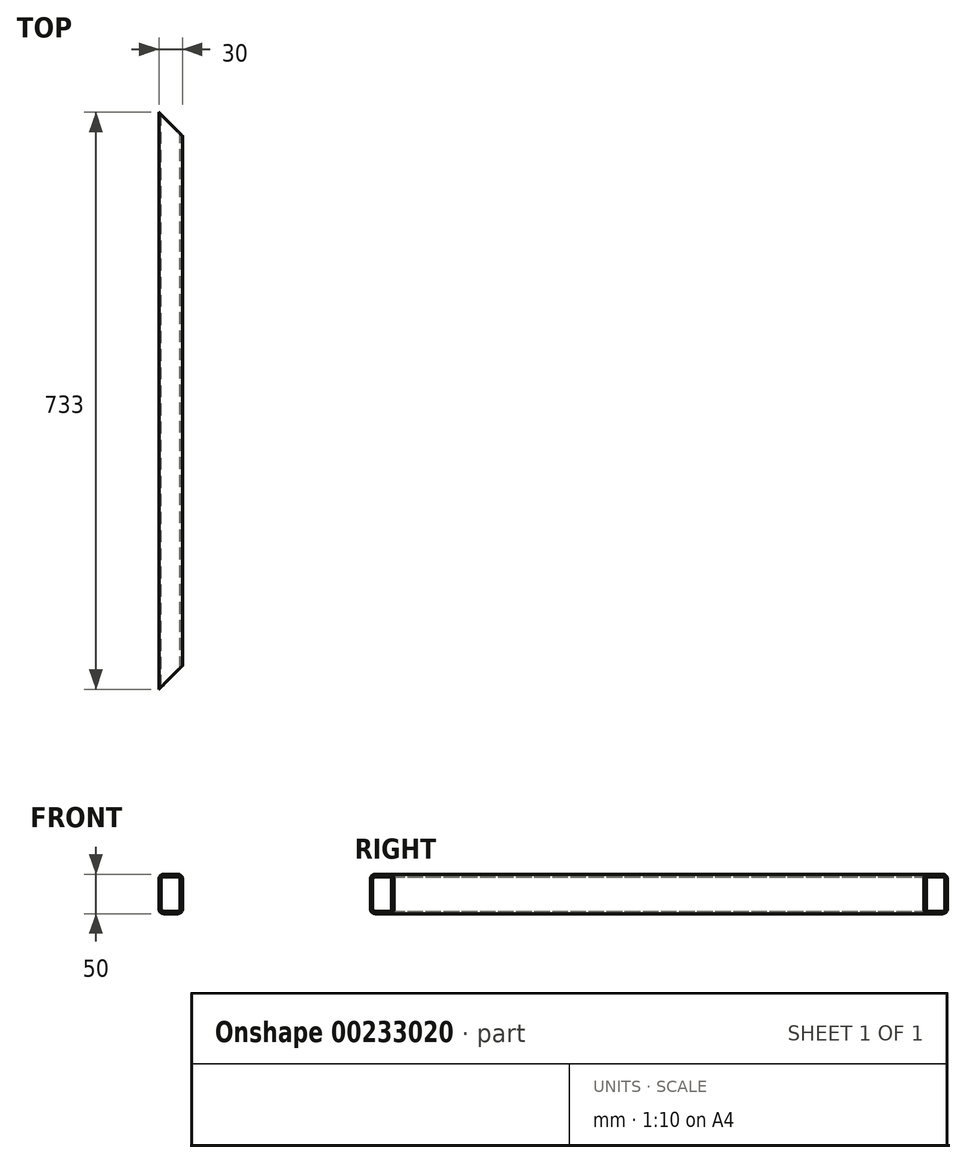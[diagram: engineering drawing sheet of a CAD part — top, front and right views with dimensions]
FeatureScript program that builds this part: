
annotation { "Feature Type Name" : "Feature", "Feature Type Description" : "" }
export const myFeature = defineFeature(function(context is Context, id is Id, definition is map)
    precondition{}
    {
        {
            var Q0;
            Q0=qCreatedBy(makeId("Front.planeOp"),FACE);
            var sketch = newSketch(context, id + "F0", { "sketchPlane" : qUnion([Q0])});
            skLineSegment(sketch, "E0.bottom", {"start": v(9, 25) * mm, "end": v(-9, 25) * mm});
            skLineSegment(sketch, "E0.top", {"start": v(9, -25) * mm, "end": v(-9, -25) * mm});
            skLineSegment(sketch, "E0.left", {"start": v(15, 19) * mm, "end": v(15, -19) * mm});
            skLineSegment(sketch, "E0.right", {"start": v(-15, 19) * mm, "end": v(-15, -19) * mm});
            skPoint(sketch, "E0.middle", {"position": v(0, 0) * mm});
            skPoint(sketch, "E1.visualSharp", {"position": v(-15, 25) * mm});
            skArc(sketch, "E1.filletArc", {"start": v(-9, 25) * mm, "mid": v(-13.24, 23.24) * mm, "end": v(-15, 19) * mm});
            skPoint(sketch, "E2.visualSharp", {"position": v(-15, -25) * mm});
            skArc(sketch, "E2.filletArc", {"start": v(-15, -19) * mm, "mid": v(-13.24, -23.24) * mm, "end": v(-9, -25) * mm});
            skPoint(sketch, "E3.visualSharp", {"position": v(15, -25) * mm});
            skArc(sketch, "E3.filletArc", {"start": v(9, -25) * mm, "mid": v(13.24, -23.24) * mm, "end": v(15, -19) * mm});
            skPoint(sketch, "E4.visualSharp", {"position": v(15, 25) * mm});
            skArc(sketch, "E4.filletArc", {"start": v(15, 19) * mm, "mid": v(13.24, 23.24) * mm, "end": v(9, 25) * mm});
            skLineSegment(sketch, "E5.0", {"start": v(9, 22) * mm, "end": v(-9, 22) * mm});
            skArc(sketch, "E5.1", {"start": v(12, 19) * mm, "mid": v(11.12, 21.12) * mm, "end": v(9, 22) * mm});
            skArc(sketch, "E5.2", {"start": v(-9, 22) * mm, "mid": v(-11.12, 21.12) * mm, "end": v(-12, 19) * mm});
            skLineSegment(sketch, "E5.3", {"start": v(12, 19) * mm, "end": v(12, -19) * mm});
            skLineSegment(sketch, "E5.4", {"start": v(-12, 19) * mm, "end": v(-12, -19) * mm});
            skArc(sketch, "E5.5", {"start": v(-12, -19) * mm, "mid": v(-11.12, -21.12) * mm, "end": v(-9, -22) * mm});
            skLineSegment(sketch, "E5.6", {"start": v(9, -22) * mm, "end": v(-9, -22) * mm});
            skArc(sketch, "E5.7", {"start": v(9, -22) * mm, "mid": v(11.12, -21.12) * mm, "end": v(12, -19) * mm});
            skSolve(sketch);
        }
        {
            var Q0;
            Q0=makeQuery(id+"F0.imprint","IMPRINT",FACE,{"disambiguationData":[TD([[makeQuery(id+"F0.imprint","IMPRINT",EDGE,{"derivedFrom":sQuery(id+"F0.wireOp",EDGE,"E0.bottom")}),1.0]])]});
            extrude(context, id + "F1", {"entities" : qUnion([Q0]), "endBound" : BoundingType.SYMMETRIC, "depth" : 733 * mm});
        }
        {
            var Q0;
            Q0=makeQuery(id+"F1.opExtrude","SWEPT_FACE",FACE,{"disambiguationData":[OSD([sQuery(id+"F0.wireOp",EDGE,"E0.bottom")])]});
            var sketch = newSketch(context, id + "F2", { "sketchPlane" : qUnion([Q0])});
            skLineSegment(sketch, "E6.left", {"start": v(15, 336.5) * mm, "end": v(15, 366.5) * mm});
            skPoint(sketch, "E6.middle", {"position": v(0, 366.5) * mm});
            skLineSegment(sketch, "E7", {"start": v(15, 336.5) * mm, "end": v(-15, 366.5) * mm});
            skLineSegment(sketch, "E8", {"start": v(-15, 366.5) * mm, "end": v(15, 366.5) * mm});
            skPoint(sketch, "E8.endSnap0", {"position": v(15, 366.5) * mm});
            skPoint(sketch, "E9.orphan", {"position": v(17.67, 366.5) * mm});
            skPoint(sketch, "E6.top.end.orphan", {"position": v(-15, 396.5) * mm});
            skPoint(sketch, "E6.top.start.orphan", {"position": v(15, 396.5) * mm});
            skPoint(sketch, "E6.right.start.orphan", {"position": v(-15, 336.5) * mm});
            skLineSegment(sketch, "E10.MirrorCS", {"start": v(-15, -366.5) * mm, "end": v(15, -366.5) * mm});
            skPoint(sketch, "E11.MirrorP", {"position": v(17.67, -366.5) * mm});
            skPoint(sketch, "E12.MirrorP", {"position": v(-15, -336.5) * mm});
            skLineSegment(sketch, "E13.MirrorCS", {"start": v(15, -336.5) * mm, "end": v(15, -366.5) * mm});
            skLineSegment(sketch, "E14.MirrorCS", {"start": v(15, -336.5) * mm, "end": v(-15, -366.5) * mm});
            skPoint(sketch, "E15.MirrorP", {"position": v(15, -366.5) * mm});
            skPoint(sketch, "E16.MirrorP", {"position": v(0, -366.5) * mm});
            skSolve(sketch);
        }
        {
            var Q0;
            {var subQ0=sQuery(id+"F2.wireOp",EDGE,"E10.MirrorCS");var subQ1=makeQuery(id+"F1.opExtrude","SWEPT_EDGE",EDGE,{"disambiguationData":[OSD([sQuery(id+"F0.wireOp",EDGE,"E0.bottom"),sQuery(id+"F0.wireOp",EDGE,"E1.filletArc")])]});var subQ2=makeQuery(id+"F2.imprint","INTERSECT",VERTEX,{"derivedFrom":[subQ1,subQ0]});var subQ3=sQuery(id+"F2.wireOp",EDGE,"E14.MirrorCS");var subQ4=makeQuery(id+"F2.imprint","INTERSECT",VERTEX,{"derivedFrom":[subQ0,subQ3]});Q0=makeQuery(id+"F2.imprint","IMPRINT",FACE,{"disambiguationData":[TD([[makeQuery(id+"F2.imprint","IMPRINT",EDGE,{"disambiguationData":[TD([[subQ2,1.0],[subQ4,-1.0]])],"derivedFrom":subQ0}),1.0]])]});}
            var Q1;
            {var subQ0=sQuery(id+"F2.wireOp",EDGE,"E10.MirrorCS");var subQ1=sQuery(id+"F0.wireOp",EDGE,"E0.bottom");var subQ2=makeQuery(id+"F1.opExtrude","SWEPT_EDGE",EDGE,{"disambiguationData":[OSD([subQ1,sQuery(id+"F0.wireOp",EDGE,"E4.filletArc")])]});var subQ3=makeQuery(id+"F2.imprint","INTERSECT",VERTEX,{"derivedFrom":[subQ2,subQ0]});var subQ4=makeQuery(id+"F1.opExtrude","SWEPT_EDGE",EDGE,{"disambiguationData":[OSD([subQ1,sQuery(id+"F0.wireOp",EDGE,"E1.filletArc")])]});var subQ5=makeQuery(id+"F2.imprint","INTERSECT",VERTEX,{"derivedFrom":[subQ4,subQ0]});Q1=makeQuery(id+"F2.imprint","IMPRINT",FACE,{"disambiguationData":[TD([[makeQuery(id+"F2.imprint","IMPRINT",EDGE,{"disambiguationData":[TD([[subQ3,-1.0],[subQ5,1.0]])],"derivedFrom":subQ0}),-1.0]])]});}
            var Q2;
            {var subQ3=sQuery(id+"F2.wireOp",EDGE,"E13.MirrorCS");Q2=makeQuery(id+"F2.imprint","IMPRINT",FACE,{"disambiguationData":[TD([[makeQuery(id+"F2.imprint","IMPRINT",EDGE,{"derivedFrom":subQ3}),-1.0]])]});}
            var Q3;
            {var subQ0=sQuery(id+"F2.wireOp",EDGE,"E8");var subQ1=sQuery(id+"F2.wireOp",EDGE,"E7");var subQ2=makeQuery(id+"F2.imprint","INTERSECT",VERTEX,{"derivedFrom":[subQ1,subQ0]});Q3=makeQuery(id+"F2.imprint","IMPRINT",FACE,{"disambiguationData":[TD([[makeQuery(id+"F2.imprint","IMPRINT",EDGE,{"disambiguationData":[TD([[subQ2,1.0]])],"derivedFrom":subQ1}),-1.0]])]});}
            var Q4;
            {var subQ0=sQuery(id+"F2.wireOp",EDGE,"E7");var subQ1=sQuery(id+"F0.wireOp",EDGE,"E0.bottom");var subQ2=makeQuery(id+"F1.opExtrude","SWEPT_EDGE",EDGE,{"disambiguationData":[OSD([subQ1,sQuery(id+"F0.wireOp",EDGE,"E4.filletArc")])]});var subQ3=makeQuery(id+"F2.imprint","INTERSECT",VERTEX,{"derivedFrom":[subQ2,subQ0]});Q4=makeQuery(id+"F2.imprint","IMPRINT",FACE,{"disambiguationData":[TD([[makeQuery(id+"F2.imprint","IMPRINT",EDGE,{"disambiguationData":[TD([[subQ3,-1.0]])],"derivedFrom":subQ0}),-1.0]])]});}
            var Q5;
            {var subQ0=sQuery(id+"F2.wireOp",EDGE,"E6.left");Q5=makeQuery(id+"F2.imprint","IMPRINT",FACE,{"disambiguationData":[TD([[makeQuery(id+"F2.imprint","IMPRINT",EDGE,{"derivedFrom":subQ0}),1.0]])]});}
            var Q6;
            Q6=makeQuery(id+"F1.opExtrude","SWEPT_FACE",FACE,{"disambiguationData":[OSD([sQuery(id+"F0.wireOp",EDGE,"E0.top")])]});
            extrude(context, id + "F3", {"entities" : qUnion([Q0, Q1, Q2, Q3, Q4, Q5]), "operationType" : NewBodyOperationType.REMOVE, "endBound" : BoundingType.UP_TO_SURFACE, "oppositeDirection" : true, "endBoundEntityFace" : qUnion([Q6]), "depth" : 25 * mm});
        }
    });
